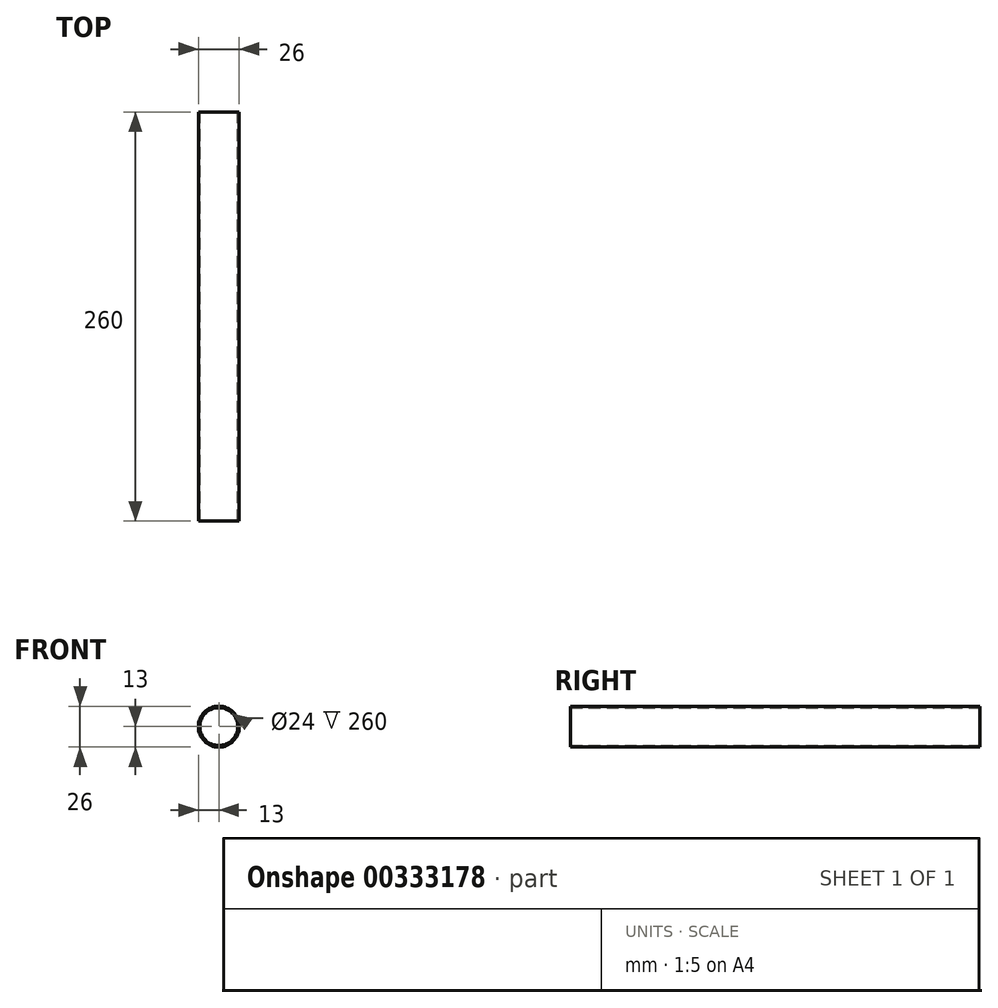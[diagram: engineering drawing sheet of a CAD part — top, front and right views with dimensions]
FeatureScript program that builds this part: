
annotation { "Feature Type Name" : "Feature", "Feature Type Description" : "" }
export const myFeature = defineFeature(function(context is Context, id is Id, definition is map)
    precondition{}
    {
        {
            var Q0;
            Q0=qCreatedBy(makeId("Front.planeOp"),FACE);
            var sketch = newSketch(context, id + "F0", { "sketchPlane" : qUnion([Q0])});
            skCircle(sketch, "E0", {"center": v(0, 0) * mm, "radius": 13 * mm});
            skCircle(sketch, "E1", {"center": v(0, 0) * mm, "radius": 12 * mm});
            skSolve(sketch);
        }
        {
            var Q0;
            Q0=qSketchRegion(id+"F0",true);
            extrude(context, id + "F1", {"entities" : qUnion([Q0]), "endBound" : BoundingType.SYMMETRIC, "depth" : 260 * mm});
        }
    });
